# Revit family: Legrand porte coffret XL³ 125
name_source: partatom
category: Equipement électrique
revit_build: Autodesk Revit 2018 (Build: 20170223_1515(x64)
units: mm (PartAtom-declared; Revit-internal decimal feet)

## family parameters
Basée sur le plan de construction = Oui
Configuration du panneau = Deux colonnes, circuits au sein
Cote de connecteur circulaire = Utiliser le diamètre
Couper avec des vides une fois chargée = Non
Numéro OmniClass = 23.80.30.11.17
Partagée = Non
Point de calcul de pièce = Non
Titre OmniClass = Distribution Boards and Control Panels
Toujours verticalement = Non
Type d'élément = Tableau de raccordement

## types (8) — shared parameters
Conditions Générale d'Utilisation = https://export.legrand.com
Couleur = RAL 9003
Elévation par défaut = 1219 mm
Fabricant = legrand
IK = 09
IP = 40
Largeur = 450 mm  [stored 1.47638 ft]
Matière = Polystyrène
Modèle = XL³ 125
porte transparente 401872 = Non
profondeur = 27 mm  [stored 0.0885827 ft]

## per-type parameters (varying)
| type | Hauteur | URL | porte blanche 401861 | porte blanche 401862 | porte blanche 401863 | porte blanche 401864 | porte transparente 401871 | porte transparente 401873 | porte transparente 401874 |
| porte blanche 401861 | 300 mm | www.bticino.com | Oui | Non | Non | Non | Non | Non | Non |
| porte blanche 401862 | 450 mm  [stored 1.47638 ft] | www.bticino.com | Non | Oui | Non | Non | Non | Non | Non |
| porte blanche 401863 | 600 mm | www.bticino.com | Non | Non | Oui | Non | Non | Non | Non |
| porte blanche 401864 | 750 mm  [stored 2.46063 ft] | www.legrand.com | Non | Non | Non | Oui | Non | Non | Non |
| porte transparente 401871 | 300 mm | www.bticino.com | Non | Non | Non | Non | Oui | Non | Non |
| porte transparente 401872 | 300 mm | www.bticino.com | Non | Non | Non | Non | Non | Non | Non |
| porte transparente 401873 | 300 mm | www.bticino.com | Non | Non | Non | Non | Non | Oui | Non |
| porte transparente 401874 | 300 mm | www.bticino.com | Non | Non | Non | Non | Non | Non | Oui |

note: [stored X ft] marks values corroborated as IEEE doubles in the binary element streams (Revit-internal decimal feet)
